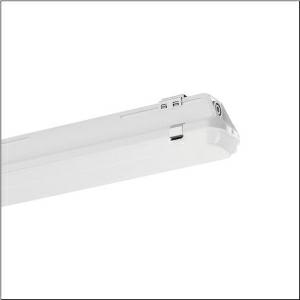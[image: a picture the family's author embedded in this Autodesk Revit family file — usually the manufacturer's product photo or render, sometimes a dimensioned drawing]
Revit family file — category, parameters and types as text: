
# Revit family: monsun_r__21_emergency_51fb10dl447k3h_80f6
name_source: partatom
category: Lighting Fixtures
units: mm (PartAtom-declared; Revit-internal decimal feet)

## family parameters
Cut with Voids When Loaded = No
Host = Face
Light Source = No
Part Type = Normal
Room Calculation Point = No
Round Connector Dimension = Use Diameter
Shared = No

## types (1)
- --- (1 x LED, 4330 lm, 28.1 W, 4000K)
    Apparent Load = 28 VA
    CIE Flux Codes = 46 76 93 94 100
    Color Rendering = 80
    Color Temperature = 4000K
    Default Elevation = 1800 mm
    Description = Monsun® 21 emergency, damp-proof luminaire, chain hanger, primary optical cover: enclosure, of PMMA, light emission: direct distribution, primary light characteristic: symmetric, installation type: vertical mounting, horizontal mounting, surface-mounted, suspended mounting, LED, rated luminous flux: 4.330lm, luminous efficacy: 178lm/W, light colour: 840, colour temperature: 4000K, control gear: DALI 2, with terminal, 5-pole, max. 2.5mm², mains connection: 220..240V, AC, 50/60Hz, rated input power: 28W, control gear: single battery element, battery: LiFePO4, 9Ah, housing, of glass-fibre reinforced plastic, uncoated, bright grey, incl. chain hanger, length: 1.299mm, width: 90mm, height: 88mm, clip for enclosure, of stainless steel (V2A), ceiling mounting element, of stainless steel (V2A), chain hanger, of stainless steel (V2A), protection rating (complete): IP66, insulation class (complete): insulation class I (protective earthing), certification: CE, UKCA, protection symbol: D, impact resistance: IK04, permissible operating ambient temperature: +5..+25°C, standard: EN 50419, EN 60598-2-1, corresponds to IFS (International Featured Standards) requirements for safety and quality in the food industry, for indoor or canopied outdoor use, no direct snow, no direct sun, no direct rain, LABS conformity tested according to VDMA 24364:2018-05, contact your sales advisor before using the luminaires in applications with unclear chemical exposure, large temperature fluctuations or condensation-forming humidity, packaging unit: 1 piece
    Height = 88 mm
    Lamp = 1 x LED
    Lamp Light Flux = 4330 lm
    Lamp Power = 28.1 W
    Lamp count = 1
    Length = 1299 mm
    Luminous efficacy = 154 lm/W
    Manufacturer = Siteco
    ModVariant = No
    Model = 51FB10DL447K3H
    Mounting Place = Ceiling
    Mounting Type = Surface mounted
    Number of Poles = 1
    OnlyDefault = Yes
    Power Factor = 1
    Product Name = Monsun® 21 emergency
    Product group = damp-proof luminaire
    ProductGroupID = 300
    Protection Class = Protection class I
    Protection Degree = IP 66
    RLX_Detail_Level = 1
    RLX_Emergency_Light_Flux = 0 lm
    RLX_Emergency_Type = 0
    RLX_Emergency_Type_DB = No
    RlxData = <blob elided: 93741 chars, md5=1311ba81>
    Socket = socket
    Standby Power = 0 W
    System Light Flux = 4330 lm
    System Power = 28 W
    Type Comments = : luminous flux: 100 % | dim-lin: 254 | 164 mA
    Type Image = l_1319656.jpg
    URL = http://relux.com
    VarID = @adj_022448
    Voltage = 0 V
    Weight = 0.00 kg
    Width = 90 mm

## geometry (parser evidence)
native form markers: Blend x4, Sweep x15
no freeform markers — native parametric forms only
